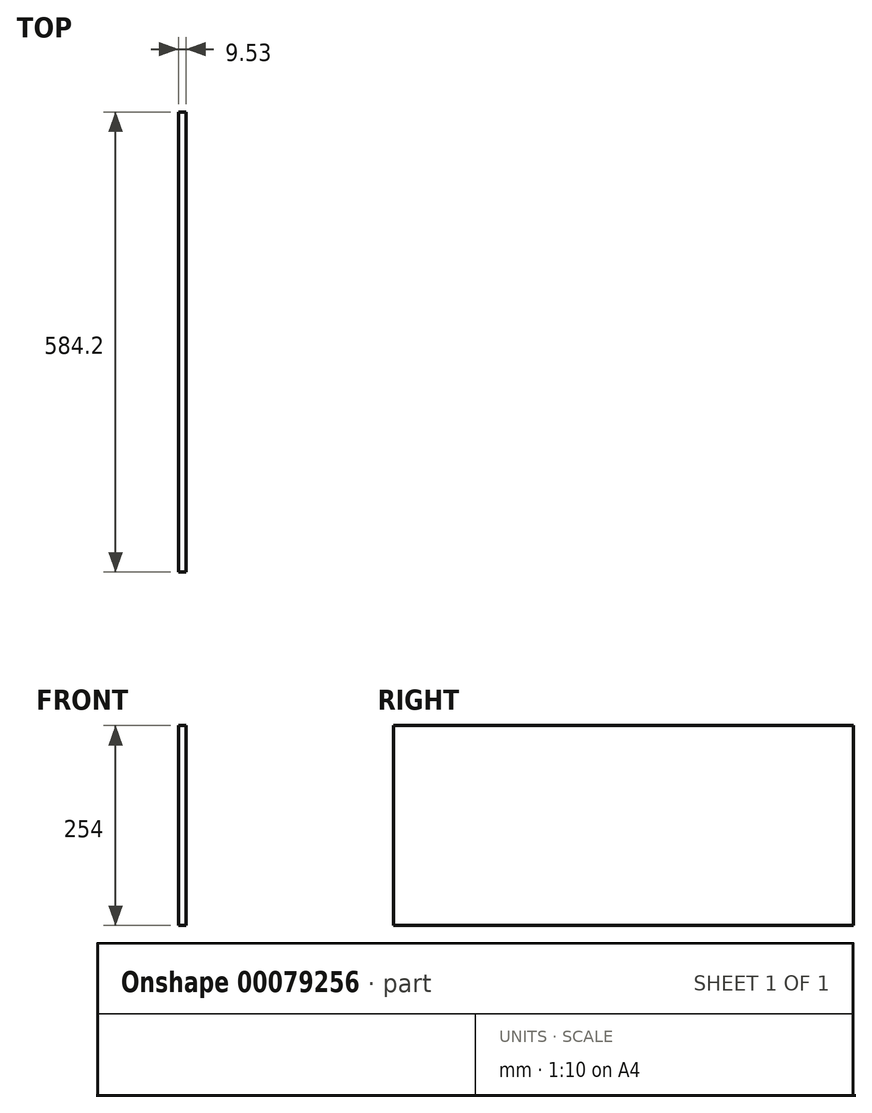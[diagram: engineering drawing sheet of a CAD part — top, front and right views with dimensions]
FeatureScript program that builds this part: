
annotation { "Feature Type Name" : "Feature", "Feature Type Description" : "" }
export const myFeature = defineFeature(function(context is Context, id is Id, definition is map)
    precondition{}
    {
        {
            var Q0;
            Q0=qCreatedBy(makeId("Right.planeOp"),FACE);
            var sketch = newSketch(context, id + "F0", { "sketchPlane" : qUnion([Q0])});
            skLineSegment(sketch, "E0.bottom", {"start": v(0, 0) * mm, "end": v(584.2, 0) * mm});
            skLineSegment(sketch, "E0.top", {"start": v(0, 254) * mm, "end": v(584.2, 254) * mm});
            skLineSegment(sketch, "E0.left", {"start": v(0, 0) * mm, "end": v(0, 254) * mm});
            skLineSegment(sketch, "E0.right", {"start": v(584.2, 0) * mm, "end": v(584.2, 254) * mm});
            skSolve(sketch);
        }
        {
            var Q0;
            Q0=makeQuery(id+"F0.imprint","IMPRINT",FACE,{"disambiguationData":[TD([[makeQuery(id+"F0.imprint","IMPRINT",EDGE,{"derivedFrom":sQuery(id+"F0.wireOp",EDGE,"E0.bottom")}),1.0]])]});
            extrude(context, id + "F1", {"entities" : qUnion([Q0]), "depth" : 9.52 * mm});
        }
    });
